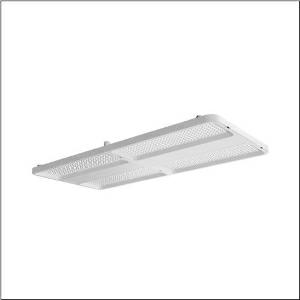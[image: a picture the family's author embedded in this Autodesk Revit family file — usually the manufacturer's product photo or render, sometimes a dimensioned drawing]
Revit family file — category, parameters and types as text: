
# Revit family: highbay_21_maxi_52hn11db4qda
name_source: partatom
category: Lighting Fixtures
units: mm (PartAtom-declared; Revit-internal decimal feet)

## family parameters
Cut with Voids When Loaded = No
Host = Face
Light Source = No
Part Type = Normal
Room Calculation Point = No
Round Connector Dimension = Use Diameter
Shared = No

## types (1)
- --- (1 x LED, 5840 lm, 31.4 W, 4000K)
    Apparent Load = 31 VA
    CIE Flux Codes = 89 97 99 100 100
    Color Rendering = 80
    Color Temperature = 4000K
    Default Elevation = 1800 mm
    Description = high bay luminaire Highbay 21 maxi; direct symmetric narrow distribution, light control with lens of PMMA; UGR ≤ 22 (X = 4H | Y = 8H | S = 0.25H | reflection values 70/50/20); luminous flux: 38.000lm; light colour: 840, colour temperature: 4000K, MacAdam ≤ 3 SDCM (initial), colour rendering: CRI > 80; luminous efficacy: 192,2lm/W; rated service life: 75.000h (L80) at AT= ta max; control: DALI 2; luminaire connection: terminal, 5-pole, max. 2.5mm² (cable entry for one cable, Ø 8.5..16mm); mains connection: 230..240V, AC/DC 0/50..60Hz; connected load: 197,7W; protection rating (complete): IP66; insulation class (complete): insulation class I (protective earthing); protection symbol: D; impact resistance: IK08; certification: CE, ENEC, VDE, UKCA; luminaire for central battery installations according to EN 60598-2-22, internal wiring halogen-free; luminaire LABS conformity tested according to VDMA 24364:2018-05; Suitable for use in the food industry according to the specifications of IFS-Food, HACCP and/or BRC; housing frame of high-performance plastic PA6, matt traffic white (RAL 9016); cover of PMMA; dimension (LxWxH): 946 x 442 x 72mm; permissible operating ambient temperature: -40..+60°C (reducing of maximum allowable ambient temperature of 5°C with ceiling mounting); packaging unit: 1 piece; (delivery without accessories; please order mounting accessories separately)
    Height = 72 mm  [stored 0.23622 ft]
    Lamp = 1 x LED
    Lamp Light Flux = 5840 lm
    Lamp Power = 31.4 W
    Lamp count = 1
    Length = 946 mm
    Luminous efficacy = 186 lm/W
    Manufacturer = Siteco
    ModVariant = No
    Model = 52HN11DB4QDA
    Mounting Place = Ceiling
    Mounting Type = Pendant
    Number of Poles = 1
    OnlyDefault = Yes
    Power Factor = 1
    Product Name = Highbay 21 maxi
    Product group = high bay luminaire
    ProductGroupID = 902
    Protection Class = Protection class I
    Protection Degree = IP 66
    RLX_Detail_Level = 1
    RLX_Emergency_Light_Flux = 0 lm
    RLX_Emergency_Type = 0
    RLX_Emergency_Type_DB = No
    RlxData = <blob elided: 128509 chars, md5=eed9e513>
    Socket = socket
    Standby Power = 0 W
    System Light Flux = 5840 lm
    System Power = 31 W
    Type Comments = : DC mode (central or group accumulator) initial emergency light level
    Type Image = l_1363244.jpg
    URL = http://relux.com
    VarID = @adj_016209
    Voltage = 0 V
    Weight = 0.00 kg
    Width = 442 mm

note: [stored X ft] marks values corroborated as IEEE doubles in the binary element streams (Revit-internal decimal feet)

## geometry (parser evidence)
native form markers: Blend x4, Sweep x9
no freeform markers — native parametric forms only
